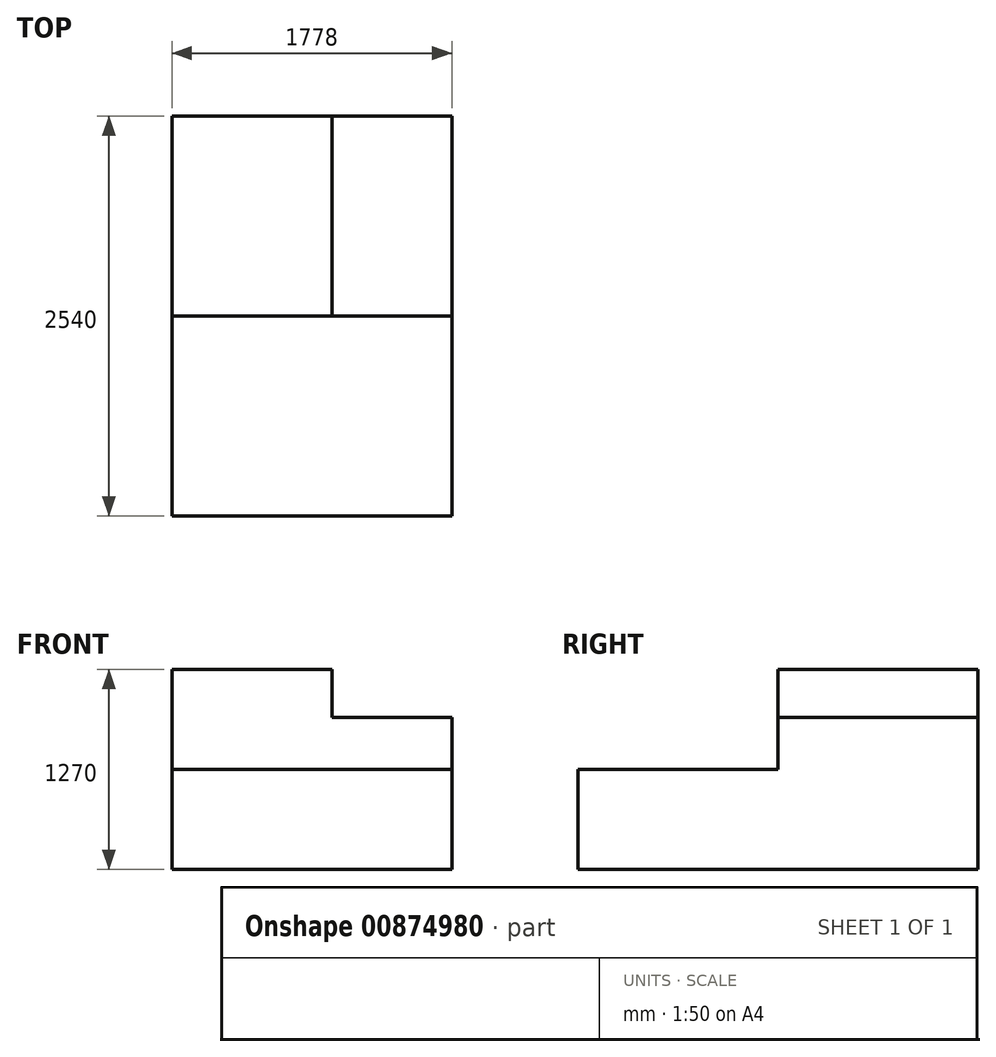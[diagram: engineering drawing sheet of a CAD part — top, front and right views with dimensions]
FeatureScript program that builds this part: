
annotation { "Feature Type Name" : "Feature", "Feature Type Description" : "" }
export const myFeature = defineFeature(function(context is Context, id is Id, definition is map)
    precondition{}
    {
        {
            var Q0;
            Q0=qCreatedBy(makeId("Front.planeOp"),FACE);
            var sketch = newSketch(context, id + "F0", { "sketchPlane" : qUnion([Q0])});
            skLineSegment(sketch, "E0.bottom", {"start": v(-153.83, -85.8) * mm, "end": v(1624.17, -85.8) * mm});
            skLineSegment(sketch, "E0.top", {"start": v(-153.83, 549.2) * mm, "end": v(1624.17, 549.2) * mm});
            skLineSegment(sketch, "E0.left", {"start": v(-153.83, -85.8) * mm, "end": v(-153.83, 549.2) * mm});
            skLineSegment(sketch, "E0.right", {"start": v(1624.17, -85.8) * mm, "end": v(1624.17, 549.2) * mm});
            skSolve(sketch);
        }
        {
            var Q0;
            Q0=makeQuery(id+"F0.imprint","IMPRINT",FACE,{"disambiguationData":[TD([[makeQuery(id+"F0.imprint","IMPRINT",EDGE,{"derivedFrom":sQuery(id+"F0.wireOp",EDGE,"E0.bottom")}),1.0]])]});
            extrude(context, id + "F1", {"entities" : qUnion([Q0]), "oppositeDirection" : true, "depth" : 2540 * mm, "offsetDistance" : 25.4 * mm});
        }
        {
            var Q0;
            Q0=makeQuery(id+"F1.opExtrude","SWEPT_FACE",FACE,{"disambiguationData":[OSD([sQuery(id+"F0.wireOp",EDGE,"E0.top")])]});
            var sketch = newSketch(context, id + "F2", { "sketchPlane" : qUnion([Q0])});
            skLineSegment(sketch, "E1.bottom", {"start": v(-153.83, 2540) * mm, "end": v(862.17, 2540) * mm});
            skLineSegment(sketch, "E1.top", {"start": v(-153.83, 1270) * mm, "end": v(862.17, 1270) * mm});
            skLineSegment(sketch, "E1.left", {"start": v(-153.83, 2540) * mm, "end": v(-153.83, 1270) * mm});
            skLineSegment(sketch, "E1.right", {"start": v(862.17, 2540) * mm, "end": v(862.17, 1270) * mm});
            skSolve(sketch);
        }
        {
            var Q0;
            Q0=makeQuery(id+"F2.imprint","IMPRINT",FACE,{"disambiguationData":[TD([[makeQuery(id+"F2.imprint","IMPRINT",EDGE,{"derivedFrom":sQuery(id+"F2.wireOp",EDGE,"E1.bottom")}),-1.0]])]});
            extrude(context, id + "F3", {"entities" : qUnion([Q0]), "operationType" : NewBodyOperationType.ADD, "depth" : 635 * mm, "offsetDistance" : 25.4 * mm});
        }
        {
            var Q0;
            Q0=makeQuery(id+"F1.opExtrude","SWEPT_FACE",FACE,{"disambiguationData":[OSD([sQuery(id+"F0.wireOp",EDGE,"E0.top")])]});
            var sketch = newSketch(context, id + "F4", { "sketchPlane" : qUnion([Q0])});
            skLineSegment(sketch, "E2.bottom", {"start": v(1624.17, 2540) * mm, "end": v(862.17, 2540) * mm});
            skLineSegment(sketch, "E2.top", {"start": v(1624.17, 1270) * mm, "end": v(862.17, 1270) * mm});
            skLineSegment(sketch, "E2.left", {"start": v(1624.17, 2540) * mm, "end": v(1624.17, 1270) * mm});
            skLineSegment(sketch, "E2.right", {"start": v(862.17, 2540) * mm, "end": v(862.17, 1270) * mm});
            skSolve(sketch);
        }
        {
            var Q0;
            Q0=makeQuery(id+"F4.imprint","IMPRINT",FACE,{"disambiguationData":[TD([[makeQuery(id+"F4.imprint","IMPRINT",EDGE,{"derivedFrom":sQuery(id+"F4.wireOp",EDGE,"E2.bottom")}),-1.0]])]});
            extrude(context, id + "F5", {"entities" : qUnion([Q0]), "operationType" : NewBodyOperationType.ADD, "depth" : 330.2 * mm, "offsetDistance" : 25.4 * mm});
        }
    });
